# Revit family: Haworth_APWoods_AudienceExecutive_AP_PRELIMINARY
name_source: partatom
category: Furniture
units: mm (PartAtom-declared; Revit-internal decimal feet)

## family parameters
Always vertical = Yes
Cut with Voids When Loaded = No
OmniClass Number = 23.40.20.00
OmniClass Title = General Furniture and Specialties
Room Calculation Point = No
Shared = No
Work Plane-Based = No

## types (3) — shared parameters
Actual Depth = 2230 mm
Actual Height = 680 mm  [stored 2.23097 ft]
Actual Width = 2400 mm  [stored 7.87402 ft]
Assembly Code = E2020200
Cable Tray Finish = Haworth _ Paint _ Metallic Silver
Description = Haworth - AP - Audience Executive Desk
Desk Mat Finish = Haworth _ Polymer _ Black
Glide Finish = Haworth _ Polymer _ Black
Grommet Finish = Haworth _ Polymer _ Black
Manufacturer = Haworth
Model = WOAUEWOX
Size = Verify Final Dim. w/ Haworth
Trim Finish = Haworth _ Polymer _ Undecided
URL = https://www.haworth.com
URL - Product = https://www.haworth.com
Version = 1
Warranty = http://www.haworth.com

## type names (no varying parameters)
- WOAUEWOE
- WOAUEWOD
- WOAUEWOA

note: [stored X ft] marks values corroborated as IEEE doubles in the binary element streams (Revit-internal decimal feet)

## geometry (parser evidence)
native form markers: Sweep x5
no freeform markers — native parametric forms only
